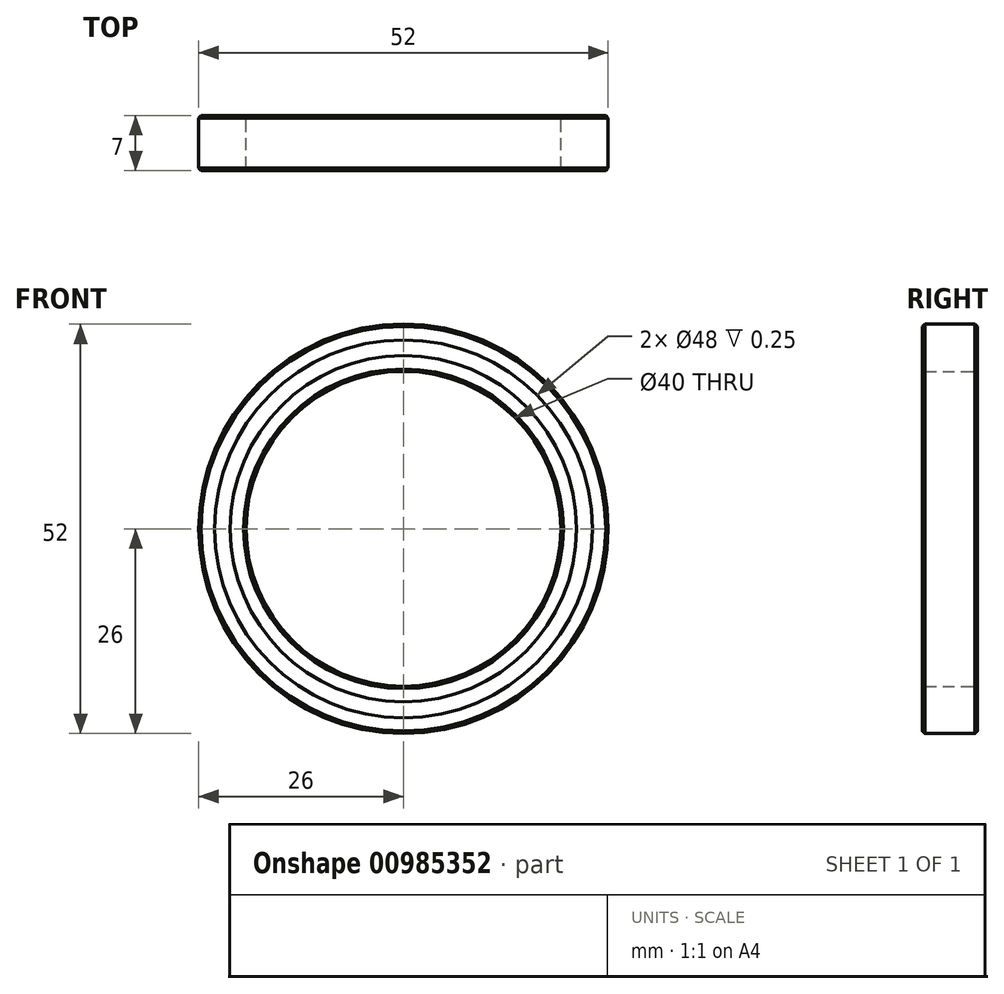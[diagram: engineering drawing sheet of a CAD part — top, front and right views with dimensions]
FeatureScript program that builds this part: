
annotation { "Feature Type Name" : "Feature", "Feature Type Description" : "" }
export const myFeature = defineFeature(function(context is Context, id is Id, definition is map)
    precondition{}
    {
        {
            var Q0;
            Q0=qCreatedBy(makeId("Front.planeOp"),FACE);
            var sketch = newSketch(context, id + "F0", { "sketchPlane" : qUnion([Q0])});
            skCircle(sketch, "E0", {"center": v(0, 0) * mm, "radius": 26 * mm});
            skCircle(sketch, "E1", {"center": v(0, 0) * mm, "radius": 24 * mm});
            skCircle(sketch, "E2", {"center": v(0, 0) * mm, "radius": 22 * mm});
            skCircle(sketch, "E3", {"center": v(0, 0) * mm, "radius": 20 * mm});
            skSolve(sketch);
        }
        {
            var Q0;
            Q0=makeQuery(id+"F0.imprint","IMPRINT",FACE,{"disambiguationData":[TD([[makeQuery(id+"F0.imprint","IMPRINT",EDGE,{"derivedFrom":sQuery(id+"F0.wireOp",EDGE,"E0")}),1.0]])]});
            var Q1;
            Q1=makeQuery(id+"F0.imprint","IMPRINT",FACE,{"disambiguationData":[TD([[makeQuery(id+"F0.imprint","IMPRINT",EDGE,{"derivedFrom":sQuery(id+"F0.wireOp",EDGE,"E2")}),1.0]])]});
            extrude(context, id + "F1", {"entities" : qUnion([Q0, Q1]), "endBound" : BoundingType.SYMMETRIC, "depth" : 7 * mm});
        }
        {
            var Q0;
            Q0=makeQuery(id+"F0.imprint","IMPRINT",FACE,{"disambiguationData":[TD([[makeQuery(id+"F0.imprint","IMPRINT",EDGE,{"derivedFrom":sQuery(id+"F0.wireOp",EDGE,"E1")}),1.0]])]});
            extrude(context, id + "F2", {"entities" : qUnion([Q0]), "operationType" : NewBodyOperationType.ADD, "endBound" : BoundingType.SYMMETRIC, "depth" : 6.5 * mm});
        }
        {
            var Q0;
            Q0=makeQuery(id+"F1.opExtrude","CAP_EDGE",EDGE,{"disambiguationData":[OSD([sQuery(id+"F0.wireOp",EDGE,"E0")])],"isStart":false});
            var Q1;
            Q1=makeQuery(id+"F1.opExtrude","CAP_EDGE",EDGE,{"disambiguationData":[OSD([sQuery(id+"F0.wireOp",EDGE,"E0")])],"isStart":true});
            var Q2;
            Q2=makeQuery(id+"F1.opExtrude","CAP_EDGE",EDGE,{"disambiguationData":[OSD([sQuery(id+"F0.wireOp",EDGE,"E3")])],"isStart":false});
            var Q3;
            Q3=makeQuery(id+"F1.opExtrude","CAP_EDGE",EDGE,{"disambiguationData":[OSD([sQuery(id+"F0.wireOp",EDGE,"E3")])],"isStart":true});
            chamfer(context, id + "F3", {"entities" : qUnion([Q0, Q1, Q2, Q3]), "width" : .3 * mm, "tangentPropagation" : true});
        }
    });
